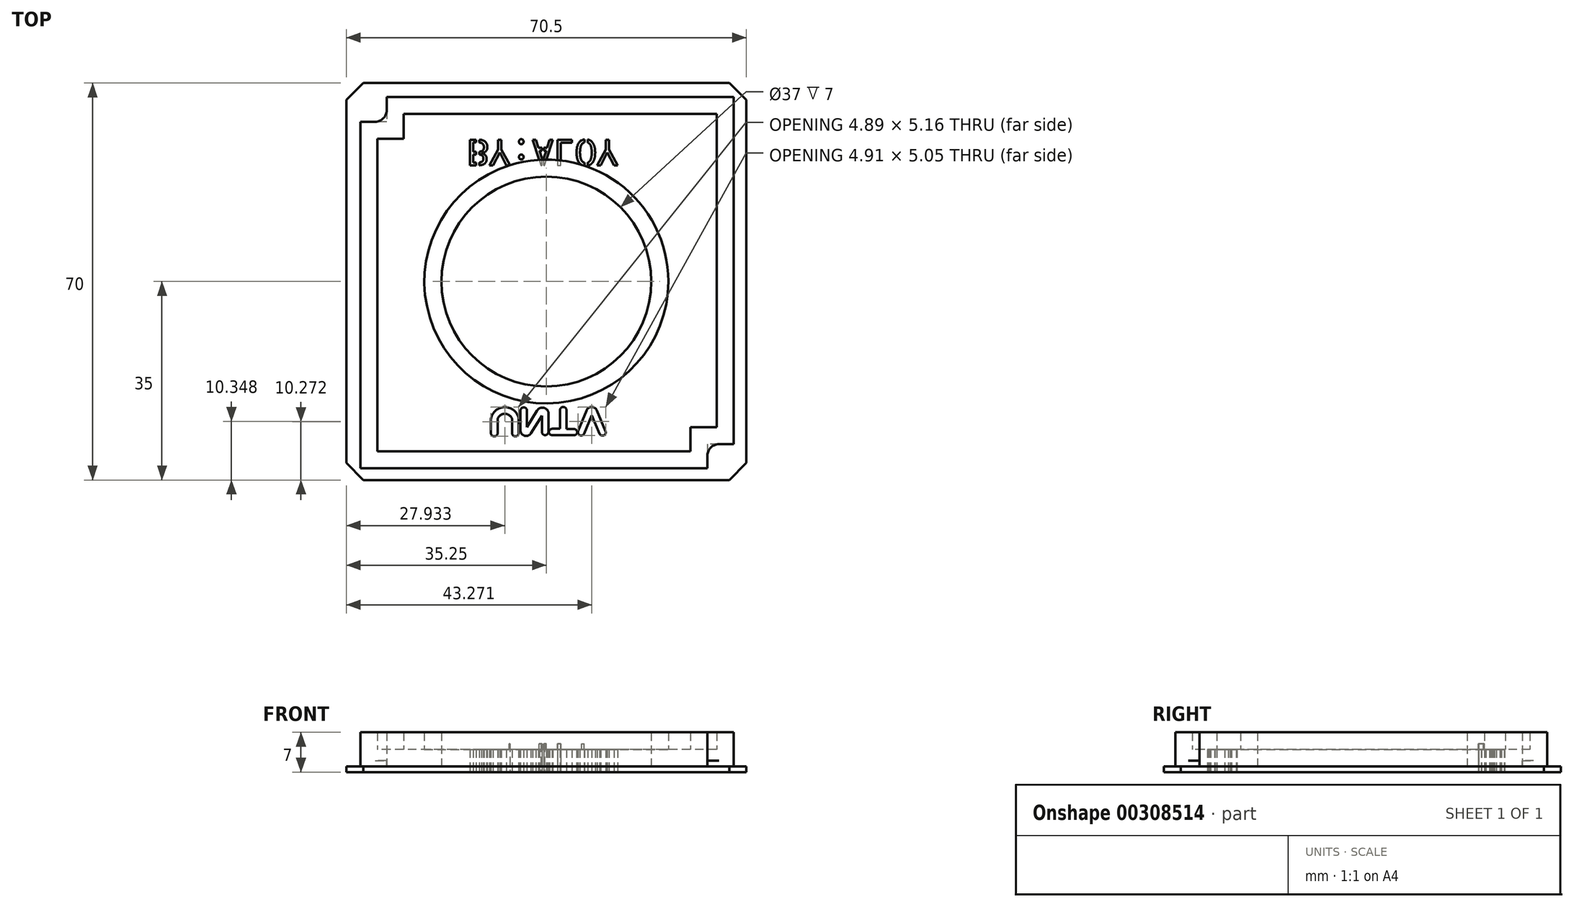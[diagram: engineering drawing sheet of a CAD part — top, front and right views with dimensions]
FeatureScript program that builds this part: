
annotation { "Feature Type Name" : "Feature", "Feature Type Description" : "" }
export const myFeature = defineFeature(function(context is Context, id is Id, definition is map)
    precondition{}
    {
        {
            var Q0;
            Q0=qCreatedBy(makeId("Top.planeOp"),FACE);
            var sketch = newSketch(context, id + "F0", { "sketchPlane" : qUnion([Q0])});
            skLineSegment(sketch, "E0.bottom", {"start": v(33, 32.55) * mm, "end": v(-28.15, 32.55) * mm});
            skLineSegment(sketch, "E0.top", {"start": v(28.4, -32.95) * mm, "end": v(-33, -32.95) * mm});
            skLineSegment(sketch, "E0.left", {"start": v(33, 32.75) * mm, "end": v(33, -28.68) * mm});
            skLineSegment(sketch, "E0.right", {"start": v(-32.8, 28.18) * mm, "end": v(-32.8, -32.95) * mm});
            skPoint(sketch, "E0.middle", {"position": v(0, 0) * mm});
            skCircle(sketch, "E1", {"center": v(0, 0) * mm, "radius": 18.5 * mm});
            skLineSegment(sketch, "E2.0", {"start": v(28.4, -28.68) * mm, "end": v(28.4, -32.95) * mm});
            skLineSegment(sketch, "E3.0", {"start": v(33, -28.68) * mm, "end": v(28.4, -28.68) * mm});
            skPoint(sketch, "E4.orphan", {"position": v(32.5, -32.75) * mm});
            skLineSegment(sketch, "E5.0", {"start": v(-28.15, 32.75) * mm, "end": v(-28.15, 28.18) * mm});
            skLineSegment(sketch, "E6.0", {"start": v(-28.15, 28.18) * mm, "end": v(-33, 28.18) * mm});
            skPoint(sketch, "E7.orphan", {"position": v(-32.5, 32.75) * mm});
            skLineSegment(sketch, "E8.bottom", {"start": v(35.25, 35) * mm, "end": v(-35.25, 35) * mm});
            skLineSegment(sketch, "E8.top", {"start": v(35.25, -35) * mm, "end": v(-35.25, -35) * mm});
            skLineSegment(sketch, "E8.left", {"start": v(35.25, 35) * mm, "end": v(35.25, -35) * mm});
            skLineSegment(sketch, "E8.right", {"start": v(-35.25, 35) * mm, "end": v(-35.25, -35) * mm});
            skPoint(sketch, "E9.orphan", {"position": v(32.5, 32.75) * mm});
            skPoint(sketch, "E10.orphan", {"position": v(-32.5, -32.75) * mm});
            skSolve(sketch);
        }
        {
            var Q0;
            Q0=makeQuery(id+"F0.imprint","IMPRINT",FACE,{"disambiguationData":[TD([[makeQuery(id+"F0.imprint","IMPRINT",EDGE,{"derivedFrom":sQuery(id+"F0.wireOp",EDGE,"E0.bottom")}),1.0]])]});
            extrude(context, id + "F1", {"entities" : qUnion([Q0]), "depth" : 5 * mm});
        }
        {
            var Q0;
            Q0=makeQuery(id+"F1.opExtrude","CAP_FACE",FACE,{"disambiguationData":[OSD([sQuery(id+"F0.wireOp",EDGE,"E0.bottom"),sQuery(id+"F0.wireOp",EDGE,"E0.top"),sQuery(id+"F0.wireOp",EDGE,"E0.left"),sQuery(id+"F0.wireOp",EDGE,"E0.right"),sQuery(id+"F0.wireOp",EDGE,"E1"),sQuery(id+"F0.wireOp",EDGE,"E2.0"),sQuery(id+"F0.wireOp",EDGE,"E3.0"),sQuery(id+"F0.wireOp",EDGE,"E5.0"),sQuery(id+"F0.wireOp",EDGE,"E6.0")])],"isStart":false});
            shell(context, id + "F2", {"entities" : qUnion([Q0]), "thickness" : 3 * mm});
        }
        {
            var Q0;
            Q0=makeQuery(id+"F1.opExtrude","SWEPT_EDGE",EDGE,{"disambiguationData":[OSD([sQuery(id+"F0.wireOp",EDGE,"E2.0"),sQuery(id+"F0.wireOp",EDGE,"E3.0")])]});
            var Q1;
            Q1=makeQuery(id+"F1.opExtrude","SWEPT_EDGE",EDGE,{"disambiguationData":[OSD([sQuery(id+"F0.wireOp",EDGE,"E5.0"),sQuery(id+"F0.wireOp",EDGE,"E6.0")])]});
            fillet(context, id + "F3", {"entities" : qUnion([Q0, Q1]), "radius" : 2 * mm, "tangentPropagation" : true, "allowEdgeOverflow" : false});
        }
        {
            var Q0;
            Q0=makeQuery(id+"F0.imprint","IMPRINT",FACE,{"disambiguationData":[TD([[makeQuery(id+"F0.imprint","IMPRINT",EDGE,{"derivedFrom":sQuery(id+"F0.wireOp",EDGE,"E0.bottom")}),-1.0]])]});
            extrude(context, id + "F4", {"entities" : qUnion([Q0]), "oppositeDirection" : true, "depth" : 2 * mm});
        }
        {
            var Q0;
            Q0=makeQuery(id+"F0.imprint","IMPRINT",FACE,{"disambiguationData":[TD([[makeQuery(id+"F0.imprint","IMPRINT",EDGE,{"derivedFrom":sQuery(id+"F0.wireOp",EDGE,"E0.bottom")}),1.0]])]});
            extrude(context, id + "F5", {"entities" : qUnion([Q0]), "operationType" : NewBodyOperationType.ADD, "oppositeDirection" : true, "depth" : 2 * mm});
        }
        {
            var Q0;
            {var subQ0=sQuery(id+"F0.wireOp",EDGE,"E6.0");var subQ1=sQuery(id+"F0.wireOp",EDGE,"E5.0");var subQ2=sQuery(id+"F0.wireOp",EDGE,"E3.0");var subQ3=sQuery(id+"F0.wireOp",EDGE,"E2.0");var subQ4=sQuery(id+"F0.wireOp",EDGE,"E0.right");var subQ5=sQuery(id+"F0.wireOp",EDGE,"E0.left");var subQ6=sQuery(id+"F0.wireOp",EDGE,"E0.top");var subQ7=sQuery(id+"F0.wireOp",EDGE,"E0.bottom");Q0=makeQuery(id+"F5.boolean.opBoolean","MERGE",FACE,{"derivedFrom":[makeQuery(id+"F4.opExtrude","CAP_FACE",FACE,{"disambiguationData":[OSD([subQ7,subQ6,subQ5,subQ4,subQ3,subQ2,subQ1,subQ0,sQuery(id+"F0.wireOp",EDGE,"E8.bottom"),sQuery(id+"F0.wireOp",EDGE,"E8.top"),sQuery(id+"F0.wireOp",EDGE,"E8.left"),sQuery(id+"F0.wireOp",EDGE,"E8.right")])],"isStart":false}),makeQuery(id+"F5.opExtrude","CAP_FACE",FACE,{"disambiguationData":[OSD([subQ7,subQ6,subQ5,subQ4,sQuery(id+"F0.wireOp",EDGE,"E1"),subQ3,subQ2,subQ1,subQ0])],"isStart":false})]});}
            var sketch = newSketch(context, id + "F6", { "sketchPlane" : qUnion([Q0])});
            skLineSegment(sketch, "E11", {"start": v(-9.76, 26.72) * mm, "end": v(-9.76, 24.23) * mm});
            skLineSegment(sketch, "E12", {"start": v(-8.59, 26.72) * mm, "end": v(-8.59, 24.23) * mm});
            skLineSegment(sketch, "E13", {"start": v(-6.05, 26.72) * mm, "end": v(-6.05, 24.23) * mm});
            skLineSegment(sketch, "E14", {"start": v(-4.87, 26.72) * mm, "end": v(-4.87, 24.23) * mm});
            skLineSegment(sketch, "E15", {"start": v(-4.56, 22.77) * mm, "end": v(-4.56, 26.23) * mm});
            skLineSegment(sketch, "E16", {"start": v(-3.4, 22.77) * mm, "end": v(-3.4, 25.67) * mm});
            skLineSegment(sketch, "E17", {"start": v(-3.4, 25.67) * mm, "end": v(-1.64, 22.77) * mm});
            skLineSegment(sketch, "E18", {"start": v(-2.72, 26.77) * mm, "end": v(-0.8, 23.64) * mm});
            skLineSegment(sketch, "E19", {"start": v(-0.8, 23.64) * mm, "end": v(-0.8, 26.51) * mm});
            skLineSegment(sketch, "E20", {"start": v(0.36, 26.51) * mm, "end": v(0.36, 23.03) * mm});
            skLineSegment(sketch, "E21", {"start": v(1.02, 27.1) * mm, "end": v(4.9, 27.1) * mm});
            skLineSegment(sketch, "E22", {"start": v(1, 25.97) * mm, "end": v(2.4, 25.97) * mm});
            skLineSegment(sketch, "E23", {"start": v(2.4, 25.97) * mm, "end": v(2.4, 22.67) * mm});
            skLineSegment(sketch, "E24", {"start": v(3.54, 22.67) * mm, "end": v(3.54, 26.03) * mm});
            skLineSegment(sketch, "E25", {"start": v(3.54, 26.03) * mm, "end": v(4.9, 26.03) * mm});
            skLineSegment(sketch, "E26", {"start": v(5.61, 26.36) * mm, "end": v(7.1, 22.72) * mm});
            skLineSegment(sketch, "E27", {"start": v(6.66, 26.85) * mm, "end": v(8, 23.62) * mm});
            skLineSegment(sketch, "E28", {"start": v(8, 23.62) * mm, "end": v(9.4, 26.9) * mm});
            skLineSegment(sketch, "E29", {"start": v(10.43, 26.38) * mm, "end": v(8.9, 22.72) * mm});
            skArc(sketch, "E30", {"start": v(7.1, 22.72) * mm, "mid": v(8, 22.12) * mm, "end": v(8.9, 22.72) * mm});
            skArc(sketch, "E31", {"start": v(6.66, 26.85) * mm, "mid": v(5.9, 27.1) * mm, "end": v(5.61, 26.36) * mm});
            skArc(sketch, "E32", {"start": v(10.43, 26.38) * mm, "mid": v(10.16, 27.12) * mm, "end": v(9.4, 26.9) * mm});
            skArc(sketch, "E33", {"start": v(4.9, 26.03) * mm, "mid": v(5.43, 26.56) * mm, "end": v(4.9, 27.1) * mm});
            skArc(sketch, "E34", {"start": v(1.02, 27.1) * mm, "mid": v(0.46, 26.55) * mm, "end": v(1, 25.97) * mm});
            skArc(sketch, "E35", {"start": v(2.4, 22.67) * mm, "mid": v(2.97, 22.1) * mm, "end": v(3.54, 22.67) * mm});
            skArc(sketch, "E36", {"start": v(0.36, 26.51) * mm, "mid": v(-0.22, 27.09) * mm, "end": v(-0.8, 26.51) * mm});
            skArc(sketch, "E37", {"start": v(-2.72, 26.77) * mm, "mid": v(-3.84, 27.2) * mm, "end": v(-4.56, 26.23) * mm});
            skArc(sketch, "E38", {"start": v(-4.56, 22.77) * mm, "mid": v(-3.99, 22.2) * mm, "end": v(-3.4, 22.77) * mm});
            skArc(sketch, "E39", {"start": v(-1.64, 22.77) * mm, "mid": v(-0.56, 22.25) * mm, "end": v(0.36, 23.03) * mm});
            skArc(sketch, "E40", {"start": v(-9.76, 24.23) * mm, "mid": v(-7.32, 22.15) * mm, "end": v(-4.87, 24.23) * mm});
            skArc(sketch, "E41", {"start": v(-8.59, 24.23) * mm, "mid": v(-7.32, 23.32) * mm, "end": v(-6.05, 24.23) * mm});
            skArc(sketch, "E42", {"start": v(-4.87, 26.72) * mm, "mid": v(-5.46, 27.3) * mm, "end": v(-6.05, 26.72) * mm});
            skArc(sketch, "E43", {"start": v(-8.59, 26.72) * mm, "mid": v(-9.17, 27.3) * mm, "end": v(-9.76, 26.72) * mm});
            skText(sketch, "E44", { "text": "BY:ALOY", "fontName": "DroidSansMono.ttf"});
            skLineSegment(sketch, "E45.bottom", {"start": v(-0.77, -20.46) * mm, "end": v(-0.45, -20.46) * mm});
            skLineSegment(sketch, "E45.left", {"start": v(-0.77, -20.46) * mm, "end": v(-0.77, -24.13) * mm});
            skLineSegment(sketch, "E45.right", {"start": v(-0.45, -20.46) * mm, "end": v(-0.45, -24.13) * mm});
            skLineSegment(sketch, "E46.bottom", {"start": v(6.71, -20.1) * mm, "end": v(7.29, -20.1) * mm});
            skLineSegment(sketch, "E46.top", {"start": v(6.71, -25.44) * mm, "end": v(7.29, -25.44) * mm});
            skLineSegment(sketch, "E46.left", {"start": v(6.71, -20.1) * mm, "end": v(6.71, -25.44) * mm});
            skLineSegment(sketch, "E46.right", {"start": v(7.29, -20.1) * mm, "end": v(7.29, -25.44) * mm});
            skLineSegment(sketch, "E47.bottom", {"start": v(-12.38, -20.2) * mm, "end": v(-11.82, -20.2) * mm});
            skLineSegment(sketch, "E47.top", {"start": v(-12.38, -25.44) * mm, "end": v(-11.82, -25.44) * mm});
            skLineSegment(sketch, "E47.left", {"start": v(-12.38, -20.2) * mm, "end": v(-12.38, -25.44) * mm});
            skLineSegment(sketch, "E47.right", {"start": v(-11.82, -20.2) * mm, "end": v(-11.82, -25.44) * mm});
            const initialGuessF6  = {"E44": [-0.0139, -0.025, 1, 0, 0.00455]};
            skSetInitialGuess(sketch, initialGuessF6);
            skSolve(sketch);
        }
        {
            var Q0;
            Q0=makeQuery(id+"F6.imprint","IMPRINT",FACE,{"disambiguationData":[TD([[makeQuery(id+"F6.imprint","IMPRINT",EDGE,{"derivedFrom":sQuery(id+"F6.wireOp",EDGE,"E11")}),1.0]])]});
            var Q1;
            Q1=makeQuery(id+"F6.imprint","IMPRINT",FACE,{"disambiguationData":[TD([[makeQuery(id+"F6.imprint","IMPRINT",EDGE,{"derivedFrom":sQuery(id+"F6.wireOp",EDGE,"E15")}),-1.0]])]});
            var Q2;
            Q2=makeQuery(id+"F6.imprint","IMPRINT",FACE,{"disambiguationData":[TD([[makeQuery(id+"F6.imprint","IMPRINT",EDGE,{"derivedFrom":sQuery(id+"F6.wireOp",EDGE,"E21")}),-1.0]])]});
            var Q3;
            Q3=makeQuery(id+"F6.imprint","IMPRINT",FACE,{"disambiguationData":[TD([[makeQuery(id+"F6.imprint","IMPRINT",EDGE,{"derivedFrom":sQuery(id+"F6.wireOp",EDGE,"E26")}),1.0]])]});
            var Q4;
            Q4=makeQuery(id+"F6.imprint","IMPRINT",FACE,{"disambiguationData":[TD([[makeQuery(id+"F6.imprint","IMPRINT",EDGE,{"derivedFrom":sQuery(id+"F6.wireOp",EDGE,"d316e64f-b6bf-4892-bafc-652fabbd4825.sketch_text.stroke-20")}),-1.0]])]});
            var Q5;
            Q5=makeQuery(id+"F6.imprint","IMPRINT",FACE,{"disambiguationData":[TD([[makeQuery(id+"F6.imprint","IMPRINT",EDGE,{"derivedFrom":sQuery(id+"F6.wireOp",EDGE,"d316e64f-b6bf-4892-bafc-652fabbd4825.sketch_text.stroke-0")}),-1.0]])]});
            var Q6;
            Q6=makeQuery(id+"F6.imprint","IMPRINT",FACE,{"disambiguationData":[TD([[makeQuery(id+"F6.imprint","IMPRINT",EDGE,{"derivedFrom":sQuery(id+"F6.wireOp",EDGE,"d316e64f-b6bf-4892-bafc-652fabbd4825.sketch_text.stroke-64")}),-1.0]])]});
            var Q7;
            Q7=makeQuery(id+"F6.imprint","IMPRINT",FACE,{"disambiguationData":[TD([[makeQuery(id+"F6.imprint","IMPRINT",EDGE,{"derivedFrom":sQuery(id+"F6.wireOp",EDGE,"d316e64f-b6bf-4892-bafc-652fabbd4825.sketch_text.stroke-58")}),-1.0]])]});
            var Q8;
            Q8=makeQuery(id+"F6.imprint","IMPRINT",FACE,{"disambiguationData":[TD([[makeQuery(id+"F6.imprint","IMPRINT",EDGE,{"derivedFrom":sQuery(id+"F6.wireOp",EDGE,"d316e64f-b6bf-4892-bafc-652fabbd4825.sketch_text.stroke-45")}),-1.0]])]});
            var Q9;
            Q9=makeQuery(id+"F6.imprint","IMPRINT",FACE,{"disambiguationData":[TD([[makeQuery(id+"F6.imprint","IMPRINT",EDGE,{"derivedFrom":sQuery(id+"F6.wireOp",EDGE,"d316e64f-b6bf-4892-bafc-652fabbd4825.sketch_text.stroke-76")}),-1.0]])]});
            var Q10;
            Q10=makeQuery(id+"F6.imprint","IMPRINT",FACE,{"disambiguationData":[TD([[makeQuery(id+"F6.imprint","IMPRINT",EDGE,{"derivedFrom":sQuery(id+"F6.wireOp",EDGE,"d316e64f-b6bf-4892-bafc-652fabbd4825.sketch_text.stroke-37")}),-1.0]])]});
            var Q11;
            Q11=makeQuery(id+"F6.imprint","IMPRINT",FACE,{"disambiguationData":[TD([[makeQuery(id+"F6.imprint","IMPRINT",EDGE,{"derivedFrom":sQuery(id+"F6.wireOp",EDGE,"d316e64f-b6bf-4892-bafc-652fabbd4825.sketch_text.stroke-41")}),-1.0]])]});
            extrude(context, id + "F7", {"entities" : qUnion([Q0, Q1, Q2, Q3, Q4, Q5, Q6, Q7, Q8, Q9, Q10, Q11]), "operationType" : NewBodyOperationType.REMOVE, "oppositeDirection" : true, "depth" : 5 * mm});
        }
        {
            var Q0;
            Q0=makeQuery(id+"F6.imprint","IMPRINT",FACE,{"disambiguationData":[TD([[makeQuery(id+"F6.imprint","IMPRINT",EDGE,{"derivedFrom":sQuery(id+"F6.wireOp",EDGE,"E44.sketch_text.stroke-23")}),-1.0]])]});
            var Q1;
            Q1=makeQuery(id+"F6.imprint","IMPRINT",FACE,{"disambiguationData":[TD([[makeQuery(id+"F6.imprint","IMPRINT",EDGE,{"derivedFrom":sQuery(id+"F6.wireOp",EDGE,"E44.sketch_text.stroke-36")}),-1.0]])]});
            var Q2;
            Q2=makeQuery(id+"F6.imprint","IMPRINT",FACE,{"disambiguationData":[TD([[makeQuery(id+"F6.imprint","IMPRINT",EDGE,{"derivedFrom":sQuery(id+"F6.wireOp",EDGE,"E44.sketch_text.stroke-32")}),-1.0]])]});
            var Q3;
            Q3=makeQuery(id+"F6.imprint","IMPRINT",FACE,{"disambiguationData":[TD([[makeQuery(id+"F6.imprint","IMPRINT",EDGE,{"derivedFrom":sQuery(id+"F6.wireOp",EDGE,"E44.sketch_text.stroke-53")}),-1.0]])]});
            var Q4;
            Q4=makeQuery(id+"F6.imprint","IMPRINT",FACE,{"disambiguationData":[TD([[makeQuery(id+"F6.imprint","IMPRINT",EDGE,{"derivedFrom":sQuery(id+"F6.wireOp",EDGE,"E44.sketch_text.stroke-71")}),-1.0]])]});
            var Q5;
            {var subQ4=sQuery(id+"F6.wireOp",EDGE,"E44.sketch_text.stroke-62");Q5=makeQuery(id+"F6.imprint","IMPRINT",FACE,{"disambiguationData":[TD([[makeQuery(id+"F6.imprint","IMPRINT",EDGE,{"derivedFrom":subQ4}),-1.0]])]});}
            var Q6;
            {var subQ6=sQuery(id+"F6.wireOp",EDGE,"E44.sketch_text.stroke-60");var subQ7=sQuery(id+"F6.wireOp",EDGE,"E44.sketch_text.stroke-59");var subQ8=makeQuery(id+"F6.imprint","INTERSECT",VERTEX,{"derivedFrom":[subQ7,subQ6]});Q6=makeQuery(id+"F6.imprint","IMPRINT",FACE,{"disambiguationData":[TD([[makeQuery(id+"F6.imprint","IMPRINT",EDGE,{"disambiguationData":[TD([[subQ8,1.0]])],"derivedFrom":subQ7}),-1.0]])]});}
            var Q7;
            {var subQ9=sQuery(id+"F6.wireOp",EDGE,"E44.sketch_text.stroke-40");Q7=makeQuery(id+"F6.imprint","IMPRINT",FACE,{"disambiguationData":[TD([[makeQuery(id+"F6.imprint","IMPRINT",EDGE,{"derivedFrom":subQ9}),-1.0]])]});}
            var Q8;
            {var subQ9=sQuery(id+"F6.wireOp",EDGE,"E44.sketch_text.stroke-42");Q8=makeQuery(id+"F6.imprint","IMPRINT",FACE,{"disambiguationData":[TD([[makeQuery(id+"F6.imprint","IMPRINT",EDGE,{"derivedFrom":subQ9}),-1.0]])]});}
            var Q9;
            {var subQ12=sQuery(id+"F6.wireOp",EDGE,"E44.sketch_text.stroke-2");Q9=makeQuery(id+"F6.imprint","IMPRINT",FACE,{"disambiguationData":[TD([[makeQuery(id+"F6.imprint","IMPRINT",EDGE,{"derivedFrom":subQ12}),-1.0]])]});}
            var Q10;
            {var subQ10=sQuery(id+"F6.wireOp",EDGE,"E44.sketch_text.stroke-10");Q10=makeQuery(id+"F6.imprint","IMPRINT",FACE,{"disambiguationData":[TD([[makeQuery(id+"F6.imprint","IMPRINT",EDGE,{"derivedFrom":subQ10}),-1.0]])]});}
            extrude(context, id + "F8", {"entities" : qUnion([Q0, Q1, Q2, Q3, Q4, Q5, Q6, Q7, Q8, Q9, Q10]), "operationType" : NewBodyOperationType.REMOVE, "oppositeDirection" : true, "depth" : 5 * mm});
        }
        {
            var Q0;
            Q0=makeQuery(id+"F4.opExtrude","SWEPT_EDGE",EDGE,{"disambiguationData":[OSD([sQuery(id+"F0.wireOp",EDGE,"E8.bottom"),sQuery(id+"F0.wireOp",EDGE,"E8.right")])]});
            var Q1;
            Q1=makeQuery(id+"F4.opExtrude","SWEPT_EDGE",EDGE,{"disambiguationData":[OSD([sQuery(id+"F0.wireOp",EDGE,"E8.bottom"),sQuery(id+"F0.wireOp",EDGE,"E8.left")])]});
            var Q2;
            Q2=makeQuery(id+"F4.opExtrude","SWEPT_EDGE",EDGE,{"disambiguationData":[OSD([sQuery(id+"F0.wireOp",EDGE,"E8.top"),sQuery(id+"F0.wireOp",EDGE,"E8.left")])]});
            var Q3;
            Q3=makeQuery(id+"F4.opExtrude","SWEPT_EDGE",EDGE,{"disambiguationData":[OSD([sQuery(id+"F0.wireOp",EDGE,"E8.top"),sQuery(id+"F0.wireOp",EDGE,"E8.right")])]});
            chamfer(context, id + "F9", {"entities" : qUnion([Q0, Q1, Q2, Q3]), "width" : 3 * mm, "tangentPropagation" : true});
        }
        {
            var Q0;
            {var subQ0=sQuery(id+"F0.wireOp",EDGE,"E6.0");var subQ1=sQuery(id+"F0.wireOp",EDGE,"E5.0");var subQ2=sQuery(id+"F0.wireOp",EDGE,"E3.0");var subQ3=sQuery(id+"F0.wireOp",EDGE,"E2.0");var subQ4=sQuery(id+"F0.wireOp",EDGE,"E1");var subQ5=sQuery(id+"F0.wireOp",EDGE,"E0.right");var subQ6=sQuery(id+"F0.wireOp",EDGE,"E0.left");var subQ7=sQuery(id+"F0.wireOp",EDGE,"E0.top");var subQ8=sQuery(id+"F0.wireOp",EDGE,"E0.bottom");Q0=makeQuery(id+"F2.opShell","OFFSET_FACE",FACE,{"disambiguationData":[OSD([subQ8,subQ7,subQ6,subQ5,subQ4,subQ3,subQ2,subQ1,subQ0]),TDD([makeQuery(id+"F1.opExtrude","CAP_FACE",FACE,{"disambiguationData":[OSD([subQ8,subQ7,subQ6,subQ5,subQ4,subQ3,subQ2,subQ1,subQ0])],"isStart":true})])]});}
            extrude(context, id + "F10", {"entities" : qUnion([Q0]), "operationType" : NewBodyOperationType.REMOVE, "oppositeDirection" : true, "depth" : 1 * mm});
        }
        {
            var Q0;
            Q0=makeQuery(id+"F0.imprint","IMPRINT",FACE,{"disambiguationData":[TD([[makeQuery(id+"F0.imprint","IMPRINT",EDGE,{"derivedFrom":sQuery(id+"F0.wireOp",EDGE,"E0.bottom")}),-1.0]])]});
            extrude(context, id + "F11", {"entities" : qUnion([Q0]), "operationType" : NewBodyOperationType.REMOVE, "oppositeDirection" : true, "depth" : 1 * mm});
        }
    });
